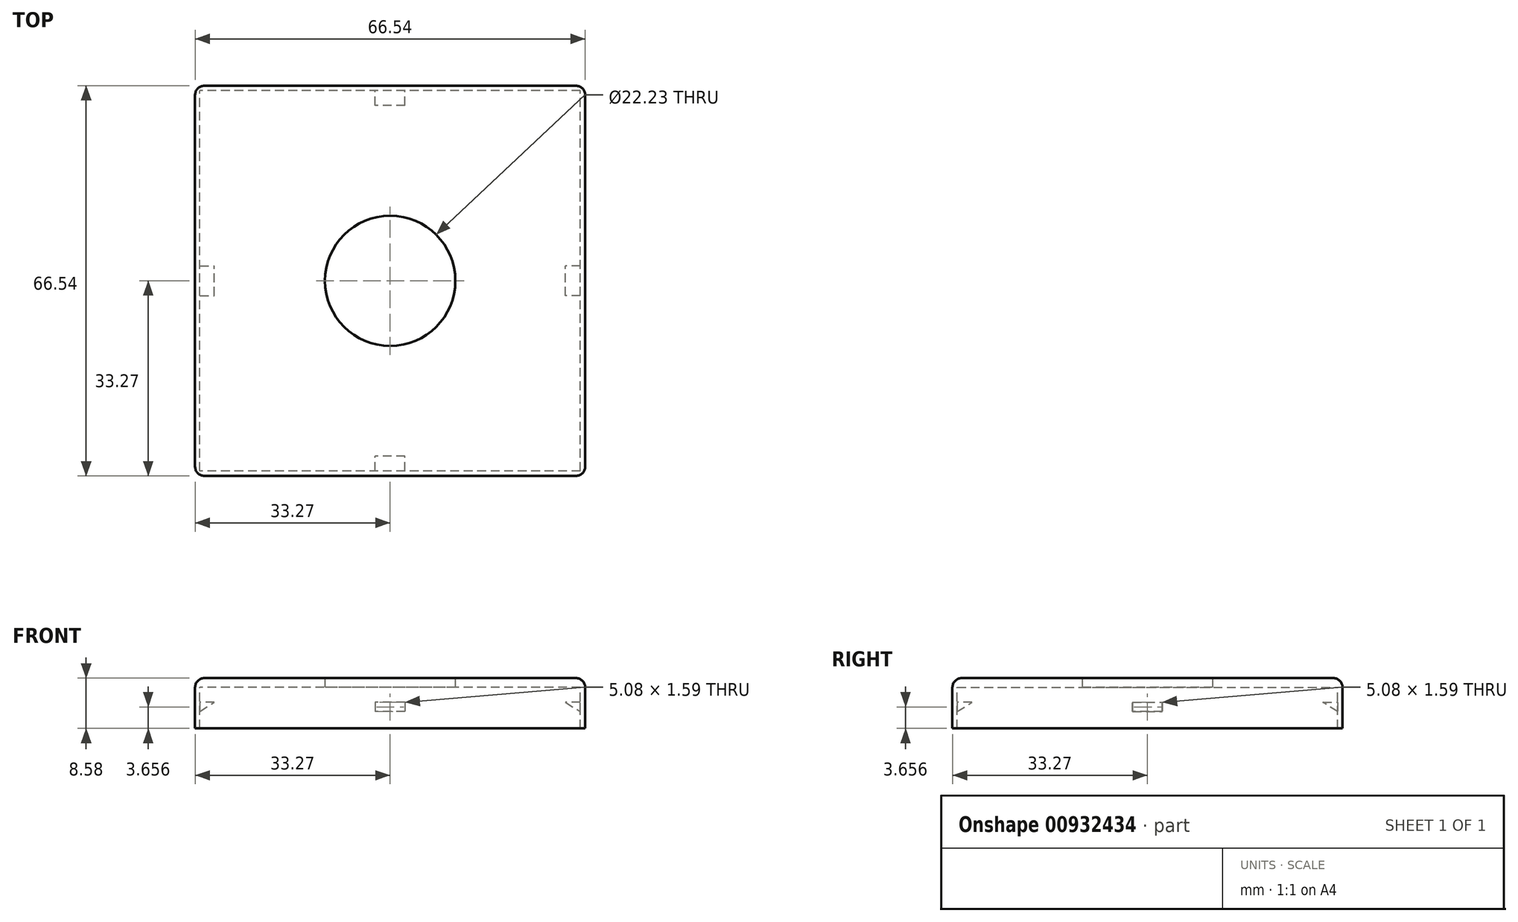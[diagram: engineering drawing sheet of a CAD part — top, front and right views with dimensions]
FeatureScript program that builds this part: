
annotation { "Feature Type Name" : "Feature", "Feature Type Description" : "" }
export const myFeature = defineFeature(function(context is Context, id is Id, definition is map)
    precondition{}
    {
        {
            var Q0;
            Q0=qCreatedBy(makeId("Top.planeOp"),FACE);
            var sketch = newSketch(context, id + "F0", { "sketchPlane" : qUnion([Q0])});
            skLineSegment(sketch, "E0.bottom", {"start": v(-33.27, 33.27) * mm, "end": v(33.27, 33.27) * mm});
            skLineSegment(sketch, "E0.top", {"start": v(-33.27, -33.27) * mm, "end": v(33.27, -33.27) * mm});
            skLineSegment(sketch, "E0.left", {"start": v(-33.27, 33.27) * mm, "end": v(-33.27, -33.27) * mm});
            skLineSegment(sketch, "E0.right", {"start": v(33.27, 33.27) * mm, "end": v(33.27, -33.27) * mm});
            skPoint(sketch, "E0.middle", {"position": v(0, 0) * mm});
            skCircle(sketch, "E1", {"center": v(0, 0) * mm, "radius": 11.11 * mm});
            skSolve(sketch);
        }
        {
            var Q0;
            Q0 = qSketchRegion(id + "F0", true);
            extrude(context, id + "F1", {"entities" : qUnion([Q0]), "depth" : 1.59 * mm, "offsetDistance" : 25.4 * mm});
        }
        {
            var Q0;
            Q0=makeQuery(id+"F1.opExtrude","CAP_FACE",FACE,{"disambiguationData":[OSD([sQuery(id+"F0.wireOp",EDGE,"E0.bottom"),sQuery(id+"F0.wireOp",EDGE,"E0.top"),sQuery(id+"F0.wireOp",EDGE,"E0.left"),sQuery(id+"F0.wireOp",EDGE,"E0.right"),sQuery(id+"F0.wireOp",EDGE,"E1")])],"isStart":true});
            var sketch = newSketch(context, id + "F2", { "sketchPlane" : qUnion([Q0])});
            skLineSegment(sketch, "E2.bottom", {"start": v(33.27, 33.27) * mm, "end": v(-33.27, 33.27) * mm});
            skLineSegment(sketch, "E2.top", {"start": v(33.27, -33.27) * mm, "end": v(-33.27, -33.27) * mm});
            skLineSegment(sketch, "E2.left", {"start": v(33.27, 33.27) * mm, "end": v(33.27, -33.27) * mm});
            skLineSegment(sketch, "E2.right", {"start": v(-33.27, 33.27) * mm, "end": v(-33.27, -33.27) * mm});
            skPoint(sketch, "E2.middle", {"position": v(0, 0) * mm});
            skLineSegment(sketch, "E3.bottom", {"start": v(32.45, 32.45) * mm, "end": v(-32.45, 32.45) * mm});
            skLineSegment(sketch, "E3.top", {"start": v(32.45, -32.45) * mm, "end": v(-32.45, -32.45) * mm});
            skLineSegment(sketch, "E3.left", {"start": v(32.45, 32.45) * mm, "end": v(32.45, -32.45) * mm});
            skLineSegment(sketch, "E3.right", {"start": v(-32.45, 32.45) * mm, "end": v(-32.45, -32.45) * mm});
            skSolve(sketch);
        }
        {
            var Q0;
            Q0 = qSketchRegion(id + "F2", true);
            extrude(context, id + "F3", {"entities" : qUnion([Q0]), "operationType" : NewBodyOperationType.ADD, "depth" : 7 * mm, "offsetDistance" : 25.4 * mm});
        }
        {
            var Q0;
            Q0=qCreatedBy(makeId("Front.planeOp"),FACE);
            var sketch = newSketch(context, id + "F4", { "sketchPlane" : qUnion([Q0])});
            skLineSegment(sketch, "E4", {"start": v(32.45, -2.54) * mm, "end": v(29.9, -2.54) * mm});
            skLineSegment(sketch, "E5", {"start": v(29.9, -2.54) * mm, "end": v(32.45, -4.13) * mm});
            skLineSegment(sketch, "E6", {"start": v(32.45, -4.13) * mm, "end": v(32.45, -2.54) * mm});
            skLineSegment(sketch, "E7", {"start": v(-29.97, -2.54) * mm, "end": v(-32.51, -2.54) * mm});
            skLineSegment(sketch, "E8", {"start": v(-32.51, -2.54) * mm, "end": v(-32.51, -4.13) * mm});
            skLineSegment(sketch, "E9", {"start": v(-32.51, -4.13) * mm, "end": v(-29.97, -2.54) * mm});
            skSolve(sketch);
        }
        {
            var Q0;
            Q0 = qSketchRegion(id + "F4", true);
            extrude(context, id + "F5", {"entities" : qUnion([Q0]), "operationType" : NewBodyOperationType.ADD, "endBound" : BoundingType.SYMMETRIC, "depth" : 5.08 * mm, "offsetDistance" : 25.4 * mm});
        }
        {
            var Q0;
            Q0=qCreatedBy(makeId("Right.planeOp"),FACE);
            var sketch = newSketch(context, id + "F6", { "sketchPlane" : qUnion([Q0])});
            skLineSegment(sketch, "E10", {"start": v(32.45, -2.54) * mm, "end": v(32.45, -4.13) * mm});
            skLineSegment(sketch, "E11", {"start": v(32.45, -4.13) * mm, "end": v(29.9, -2.54) * mm});
            skLineSegment(sketch, "E12", {"start": v(29.9, -2.54) * mm, "end": v(32.45, -2.54) * mm});
            skLineSegment(sketch, "E13", {"start": v(-29.9, -2.54) * mm, "end": v(-32.45, -2.54) * mm});
            skLineSegment(sketch, "E14", {"start": v(-32.45, -2.54) * mm, "end": v(-32.45, -4.13) * mm});
            skLineSegment(sketch, "E15", {"start": v(-32.45, -4.13) * mm, "end": v(-29.9, -2.54) * mm});
            skSolve(sketch);
        }
        {
            var Q0;
            Q0 = qSketchRegion(id + "F6", true);
            extrude(context, id + "F7", {"entities" : qUnion([Q0]), "operationType" : NewBodyOperationType.ADD, "endBound" : BoundingType.SYMMETRIC, "depth" : 5.08 * mm, "offsetDistance" : 25.4 * mm});
        }
        {
            var Q0;
            Q0=makeQuery(id+"F1.opExtrude","CAP_EDGE",EDGE,{"disambiguationData":[OSD([sQuery(id+"F0.wireOp",EDGE,"E0.left")])],"isStart":false});
            var Q1;
            Q1=makeQuery(id+"F1.opExtrude","CAP_EDGE",EDGE,{"disambiguationData":[OSD([sQuery(id+"F0.wireOp",EDGE,"E0.bottom")])],"isStart":false});
            var Q2;
            Q2=makeQuery(id+"F1.opExtrude","CAP_EDGE",EDGE,{"disambiguationData":[OSD([sQuery(id+"F0.wireOp",EDGE,"E0.right")])],"isStart":false});
            var Q3;
            Q3=makeQuery(id+"F1.opExtrude","CAP_EDGE",EDGE,{"disambiguationData":[OSD([sQuery(id+"F0.wireOp",EDGE,"E0.top")])],"isStart":false});
            var Q4;
            Q4=makeQuery(id+"F3.boolean.opBoolean","MERGE",EDGE,{"derivedFrom":[makeQuery(id+"F1.opExtrude","SWEPT_EDGE",EDGE,{"disambiguationData":[OSD([sQuery(id+"F0.wireOp",EDGE,"E0.bottom"),sQuery(id+"F0.wireOp",EDGE,"E0.left")])]}),makeQuery(id+"F3.opExtrude","SWEPT_EDGE",EDGE,{"disambiguationData":[OSD([sQuery(id+"F2.wireOp",EDGE,"E2.top"),sQuery(id+"F2.wireOp",EDGE,"E2.right")])]})]});
            var Q5;
            Q5=makeQuery(id+"F3.boolean.opBoolean","MERGE",EDGE,{"derivedFrom":[makeQuery(id+"F1.opExtrude","SWEPT_EDGE",EDGE,{"disambiguationData":[OSD([sQuery(id+"F0.wireOp",EDGE,"E0.top"),sQuery(id+"F0.wireOp",EDGE,"E0.left")])]}),makeQuery(id+"F3.opExtrude","SWEPT_EDGE",EDGE,{"disambiguationData":[OSD([sQuery(id+"F2.wireOp",EDGE,"E2.bottom"),sQuery(id+"F2.wireOp",EDGE,"E2.right")])]})]});
            var Q6;
            Q6=makeQuery(id+"F3.boolean.opBoolean","MERGE",EDGE,{"derivedFrom":[makeQuery(id+"F1.opExtrude","SWEPT_EDGE",EDGE,{"disambiguationData":[OSD([sQuery(id+"F0.wireOp",EDGE,"E0.top"),sQuery(id+"F0.wireOp",EDGE,"E0.right")])]}),makeQuery(id+"F3.opExtrude","SWEPT_EDGE",EDGE,{"disambiguationData":[OSD([sQuery(id+"F2.wireOp",EDGE,"E2.bottom"),sQuery(id+"F2.wireOp",EDGE,"E2.left")])]})]});
            var Q7;
            Q7=makeQuery(id+"F3.boolean.opBoolean","MERGE",EDGE,{"derivedFrom":[makeQuery(id+"F1.opExtrude","SWEPT_EDGE",EDGE,{"disambiguationData":[OSD([sQuery(id+"F0.wireOp",EDGE,"E0.bottom"),sQuery(id+"F0.wireOp",EDGE,"E0.right")])]}),makeQuery(id+"F3.opExtrude","SWEPT_EDGE",EDGE,{"disambiguationData":[OSD([sQuery(id+"F2.wireOp",EDGE,"E2.top"),sQuery(id+"F2.wireOp",EDGE,"E2.left")])]})]});
            fillet(context, id + "F8", {"entities" : qUnion([Q0, Q1, Q2, Q3, Q4, Q5, Q6, Q7]), "radius" : 1.59 * mm, "tangentPropagation" : true, "allowEdgeOverflow" : false});
        }
    });
